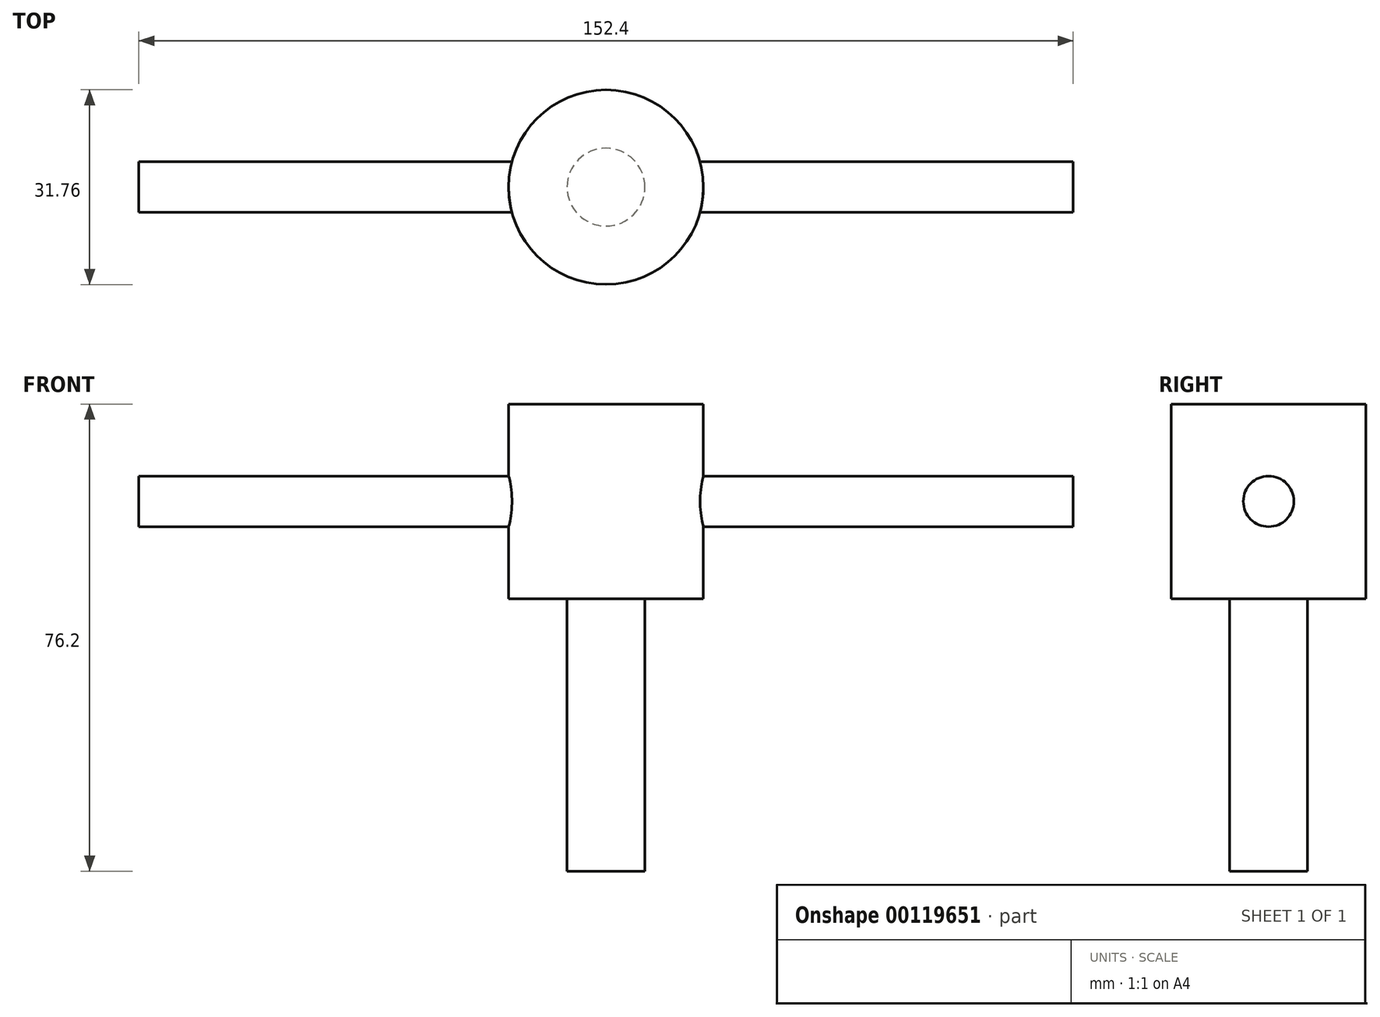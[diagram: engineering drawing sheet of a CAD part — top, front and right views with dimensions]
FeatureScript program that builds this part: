
annotation { "Feature Type Name" : "Feature", "Feature Type Description" : "" }
export const myFeature = defineFeature(function(context is Context, id is Id, definition is map)
    precondition{}
    {
        {
            var Q0;
            Q0=qCreatedBy(makeId("Top.planeOp"),FACE);
            var sketch = newSketch(context, id + "F0", { "sketchPlane" : qUnion([Q0])});
            skCircle(sketch, "E0", {"center": v(0, 0) * mm, "radius": 15.88 * mm});
            skSolve(sketch);
        }
        {
            var Q0;
            Q0 = qSketchRegion(id + "F0", true);
            extrude(context, id + "F1", {"entities" : qUnion([Q0]), "oppositeDirection" : true, "depth" : 31.75 * mm});
        }
        {
            var Q0;
            Q0=qCreatedBy(makeId("Top.planeOp"),FACE);
            var sketch = newSketch(context, id + "F2", { "sketchPlane" : qUnion([Q0])});
            skCircle(sketch, "E1", {"center": v(0, 0) * mm, "radius": 6.35 * mm});
            skSolve(sketch);
        }
        {
            var Q0;
            Q0 = qSketchRegion(id + "F2", true);
            extrude(context, id + "F3", {"entities" : qUnion([Q0]), "operationType" : NewBodyOperationType.ADD, "oppositeDirection" : true, "depth" : 76.2 * mm});
        }
        {
            var Q0;
            Q0=qCreatedBy(makeId("Right.planeOp"),FACE);
            var sketch = newSketch(context, id + "F4", { "sketchPlane" : qUnion([Q0])});
            skCircle(sketch, "E2", {"center": v(0, -15.88) * mm, "radius": 4.13 * mm});
            skSolve(sketch);
        }
        {
            var Q0;
            Q0 = qSketchRegion(id + "F4", true);
            extrude(context, id + "F5", {"entities" : qUnion([Q0]), "operationType" : NewBodyOperationType.ADD, "endBound" : BoundingType.SYMMETRIC, "depth" : 152.4 * mm});
        }
    });
